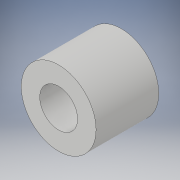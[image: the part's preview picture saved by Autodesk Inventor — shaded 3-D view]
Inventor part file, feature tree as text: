
AUTODESK INVENTOR PART (.ipt)
format: ipt  version: 2018 (Build 220112000, 112)  size: 97,280 bytes
history: native  units: in
note: dims shown in document units (in); Inventor stores cm internally (conversion verified against a paired STEP export)
features: extrude x1, sketch x1
ambient origin geometry x8: Origin, YZ Plane, XZ Plane, XY Plane, X Axis, Y Axis, Z Axis, Center Point
bodies: Solid1 (feature_tree)
feature tree (2):
  extrude  "Extrusion1"  Depth=0.6285in
  sketch  "Sketch1"  dims[d0=0.38in d1=0.75in d2=0.6285in d3=0.0in]
